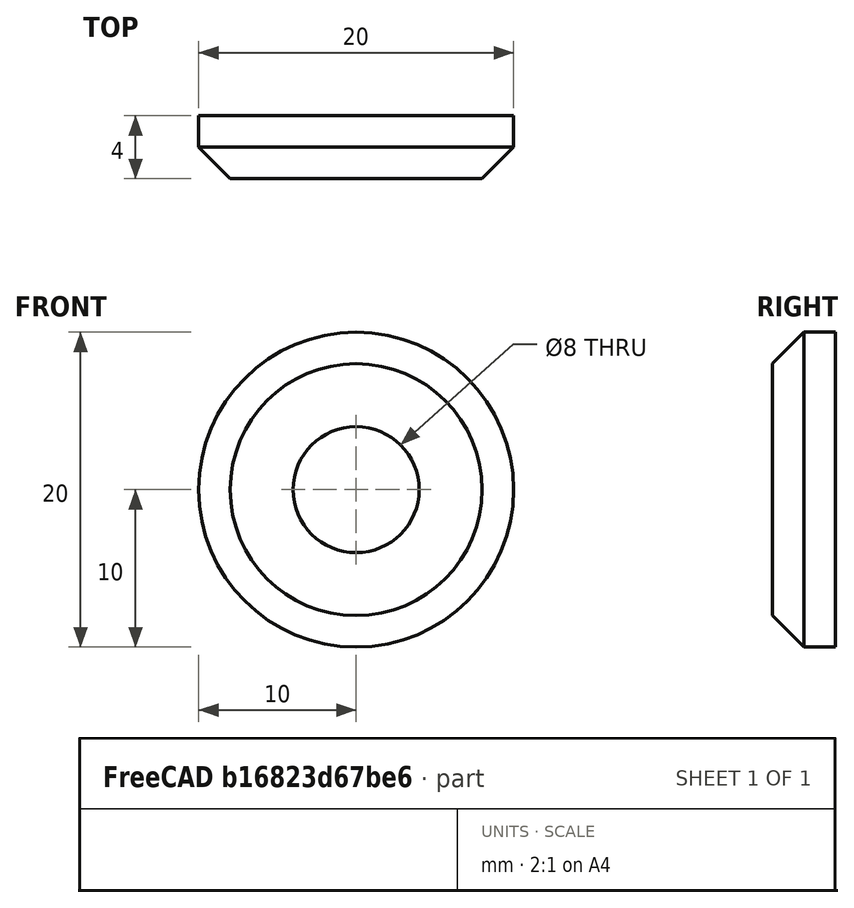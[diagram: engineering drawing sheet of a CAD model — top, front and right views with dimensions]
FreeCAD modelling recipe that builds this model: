
FCSTD DOCUMENT  (FreeCAD 0.20R28730 (Git))
Label: Tool Holder Washer
License: All rights reserved
LicenseURL: http://en.wikipedia.org/wiki/All_rights_reserved
objects: PartDesign::CoordinateSystem×2, Sketcher::SketchObject×1, PartDesign::Pad×1, PartDesign::Chamfer×1, PartDesign::Body×1
note: 8 computed .brp shape members not serialized (recipe doc carries the construction recipe); baked Part::Feature solids carry a one-line shape summary decoded from their .brp

FEATURE [Sketcher::SketchObject] Sketch
  FullyConstrained = true
  MapMode = 5
  Placement = pos=(0,0,0) rot=(1,0,0;1.5708rad)
  Support = -> [XZ_Plane]
  sketch-geometry (2):
    g0: Circle CenterX=0 CenterY=0 CenterZ=0 NormalX=0 NormalY=0 NormalZ=1 AngleXU=0 Radius=10
    g1: Circle CenterX=0 CenterY=0 CenterZ=0 NormalX=0 NormalY=0 NormalZ=1 AngleXU=0 Radius=4
  constraints (4):
    c: Coincident(g0,g-1)
    c: Coincident(g1,g0)
    c: Diameter(g1) = 8
    c: Diameter(g0) = 20
FEATURE [PartDesign::Pad] Pad
  Direction = (0,-1,2e-16)
  Length = 4
  Length2 = 10
  Placement = pos=(0,0,0) rot=(1,0,0;1.5708rad)
  Profile = -> Sketch
  ReferenceAxis = -> Sketch [N_Axis]
  Refine = true
  Type = 0
FEATURE [PartDesign::Chamfer] Chamfer
  Angle = 45
  Base = -> Pad [Edge3]
  BaseFeature = -> Pad
  ChamferType = 0
  FlipDirection = false
  Placement = pos=(0,0,0) rot=(1,0,0;1.5708rad)
  Refine = true
  Size = 2
  Size2 = 1
  SupportTransform = false
  UseAllEdges = false
FEATURE [PartDesign::CoordinateSystem] Center  label="LCS_Tool_Holder_Washer_1"
  AttacherType = Attacher::AttachEngine3D
  MapMode = 11
  Placement = pos=(0,0,0) rot=(0.57735,-0.57735,0.57735;2.0944rad)
  Support = -> [Chamfer]
FEATURE [PartDesign::CoordinateSystem] Center2  label="LCS_Tool_Holder_Washer_2"
  AttacherType = Attacher::AttachEngine3D
  MapMode = 11
  Placement = pos=(0,-4,2e-15) rot=(0.57735,-0.57735,0.57735;2.0944rad)
  Support = -> [Chamfer]
FEATURE [PartDesign::Body] Body  label="Tool_Holder_Washer"
  Group = -> [Sketch,Pad,Chamfer,Center,Center2]
  Origin = -> Origin
  Tip = -> Chamfer
